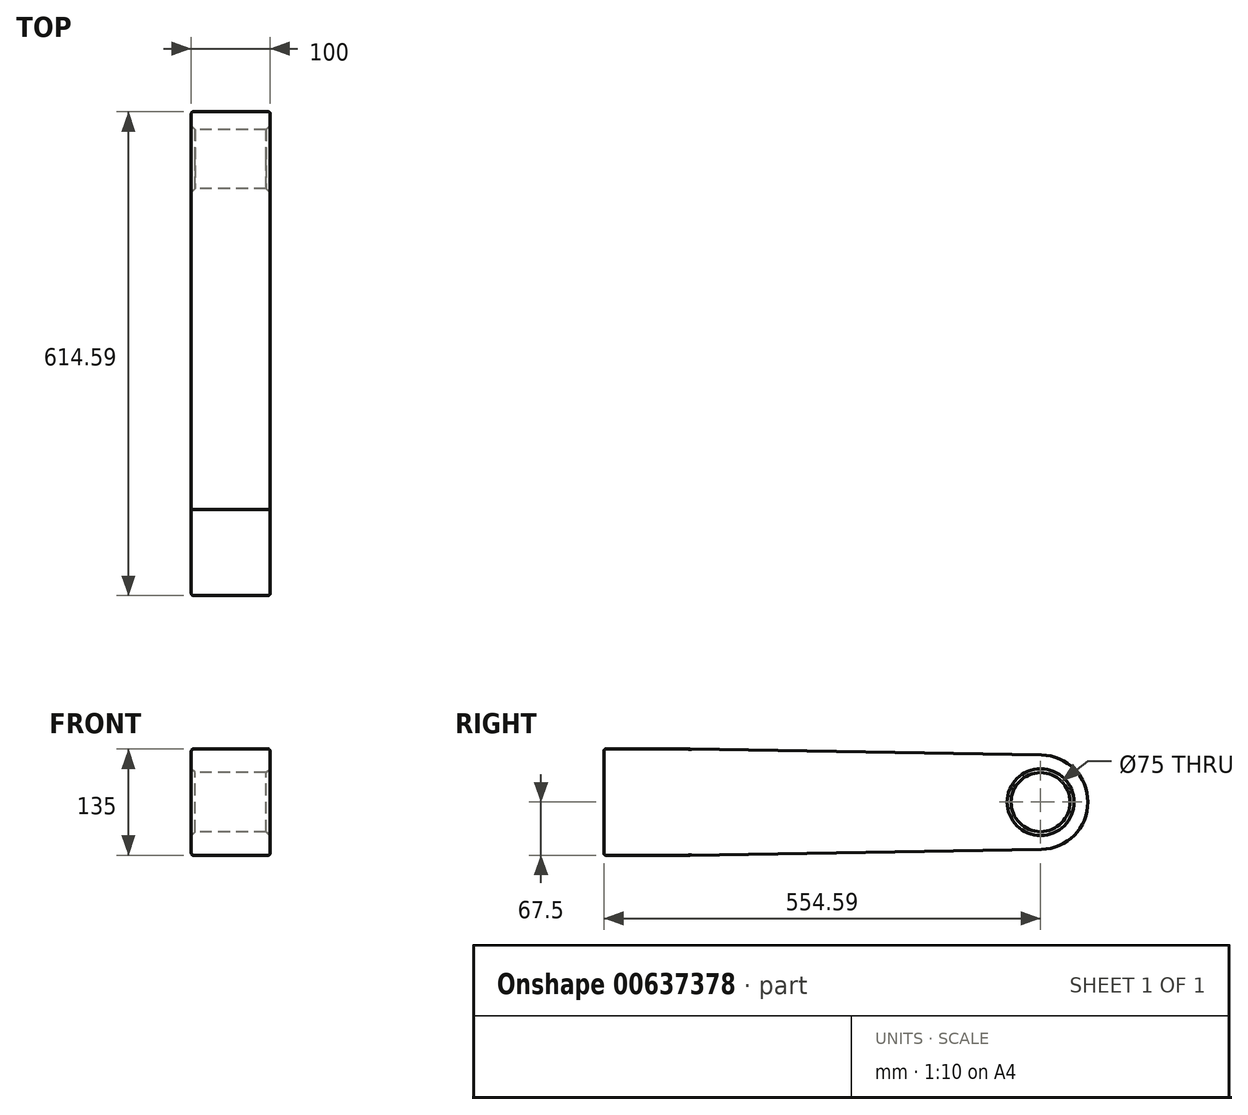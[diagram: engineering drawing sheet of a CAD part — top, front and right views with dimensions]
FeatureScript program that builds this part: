
annotation { "Feature Type Name" : "Feature", "Feature Type Description" : "" }
export const myFeature = defineFeature(function(context is Context, id is Id, definition is map)
    precondition{}
    {
        {
            var Q0;
            Q0=qCreatedBy(makeId("Right.planeOp"),FACE);
            var sketch = newSketch(context, id + "F0", { "sketchPlane" : qUnion([Q0])});
            skLineSegment(sketch, "E0.bottom", {"start": v(54.59, 67.5) * mm, "end": v(-54.59, 67.5) * mm});
            skLineSegment(sketch, "E0.top", {"start": v(54.59, -67.5) * mm, "end": v(-54.59, -67.5) * mm});
            skLineSegment(sketch, "E0.left", {"start": v(54.59, 67.5) * mm, "end": v(54.59, -67.5) * mm});
            skLineSegment(sketch, "E0.right", {"start": v(-54.59, 67.5) * mm, "end": v(-54.59, -67.5) * mm});
            skPoint(sketch, "E0.middle", {"position": v(0, 0) * mm});
            skCircle(sketch, "E1", {"center": v(500, 0) * mm, "radius": 60 * mm});
            skLineSegment(sketch, "E2", {"start": v(54.59, 67.5) * mm, "end": v(501, 60) * mm});
            skLineSegment(sketch, "E3", {"start": v(501, 60) * mm, "end": v(501, 60) * mm});
            skLineSegment(sketch, "E4", {"start": v(54.59, -67.5) * mm, "end": v(501, -60) * mm});
            skCircle(sketch, "E5", {"center": v(500, 0) * mm, "radius": 37.5 * mm});
            skSolve(sketch);
        }
        {
            var Q0;
            Q0 = qSketchRegion(id + "F0", true);
            extrude(context, id + "F1", {"entities" : qUnion([Q0]), "depth" : 100 * mm, "offsetDistance" : 25 * mm});
        }
        {
            var Q0;
            Q0=makeQuery(id+"F1.opExtrude","CAP_EDGE",EDGE,{"disambiguationData":[OSD([sQuery(id+"F0.wireOp",EDGE,"E2")])],"isStart":false});
            var Q1;
            Q1=makeQuery(id+"F1.opExtrude","CAP_EDGE",EDGE,{"disambiguationData":[OSD([sQuery(id+"F0.wireOp",EDGE,"E4")])],"isStart":false});
            var Q2;
            Q2=makeQuery(id+"F1.opExtrude","CAP_EDGE",EDGE,{"disambiguationData":[OSD([sQuery(id+"F0.wireOp",EDGE,"E0.top")])],"isStart":false});
            var Q3;
            Q3=makeQuery(id+"F1.opExtrude","CAP_EDGE",EDGE,{"disambiguationData":[OSD([sQuery(id+"F0.wireOp",EDGE,"E0.right")])],"isStart":false});
            var Q4;
            Q4=makeQuery(id+"F1.opExtrude","CAP_EDGE",EDGE,{"disambiguationData":[OSD([sQuery(id+"F0.wireOp",EDGE,"E0.bottom")])],"isStart":false});
            var Q5;
            Q5=makeQuery(id+"F1.opExtrude","CAP_EDGE",EDGE,{"disambiguationData":[OSD([sQuery(id+"F0.wireOp",EDGE,"E1")])],"isStart":false});
            var Q6;
            Q6=makeQuery(id+"F1.opExtrude","CAP_EDGE",EDGE,{"disambiguationData":[OSD([sQuery(id+"F0.wireOp",EDGE,"E2")])],"isStart":true});
            var Q7;
            Q7=makeQuery(id+"F1.opExtrude","CAP_EDGE",EDGE,{"disambiguationData":[OSD([sQuery(id+"F0.wireOp",EDGE,"E1")])],"isStart":true});
            var Q8;
            Q8=makeQuery(id+"F1.opExtrude","CAP_EDGE",EDGE,{"disambiguationData":[OSD([sQuery(id+"F0.wireOp",EDGE,"E4")])],"isStart":true});
            var Q9;
            Q9=makeQuery(id+"F1.opExtrude","CAP_EDGE",EDGE,{"disambiguationData":[OSD([sQuery(id+"F0.wireOp",EDGE,"E0.top")])],"isStart":true});
            var Q10;
            Q10=makeQuery(id+"F1.opExtrude","CAP_EDGE",EDGE,{"disambiguationData":[OSD([sQuery(id+"F0.wireOp",EDGE,"E0.right")])],"isStart":true});
            var Q11;
            Q11=makeQuery(id+"F1.opExtrude","CAP_EDGE",EDGE,{"disambiguationData":[OSD([sQuery(id+"F0.wireOp",EDGE,"E0.bottom")])],"isStart":true});
            var Q12;
            Q12=makeQuery(id+"F1.opExtrude","SWEPT_EDGE",EDGE,{"disambiguationData":[OSD([sQuery(id+"F0.wireOp",EDGE,"E0.top"),sQuery(id+"F0.wireOp",EDGE,"E0.right")])]});
            var Q13;
            Q13=makeQuery(id+"F1.opExtrude","SWEPT_EDGE",EDGE,{"disambiguationData":[OSD([sQuery(id+"F0.wireOp",EDGE,"E0.bottom"),sQuery(id+"F0.wireOp",EDGE,"E0.right")])]});
            fillet(context, id + "F2", {"entities" : qUnion([Q0, Q1, Q2, Q3, Q4, Q5, Q6, Q7, Q8, Q9, Q10, Q11, Q12, Q13]), "radius" : 2.5 * mm, "tangentPropagation" : true, "allowEdgeOverflow" : false});
        }
        {
            var Q0;
            Q0=makeQuery(id+"F1.opExtrude","CAP_EDGE",EDGE,{"disambiguationData":[OSD([sQuery(id+"F0.wireOp",EDGE,"E5")])],"isStart":false});
            var Q1;
            Q1=makeQuery(id+"F1.opExtrude","CAP_EDGE",EDGE,{"disambiguationData":[OSD([sQuery(id+"F0.wireOp",EDGE,"E5")])],"isStart":true});
            chamfer(context, id + "F3", {"entities" : qUnion([Q0, Q1]), "width" : 5 * mm, "tangentPropagation" : true});
        }
    });
